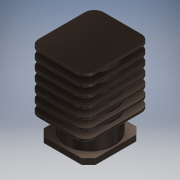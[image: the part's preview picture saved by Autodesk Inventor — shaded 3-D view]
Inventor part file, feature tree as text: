
AUTODESK INVENTOR PART (.ipt)
format: ipt  version: 2019 (Build 230136000, 136)  size: 236,544 bytes
history: native  units: mm
features: extrude x4, sketch x4, pattern_linear x1
ambient origin geometry x8: Origin, YZ Plane, XZ Plane, XY Plane, X Axis, Y Axis, Z Axis, Center Point
bodies: Solid1 (feature_tree)
feature tree (9):
  extrude  "Extrusion1"  Depth=8000.0mm TaperAngle=0.0deg
  extrude  "Extrusion2"  Depth=1000.0mm
  extrude  "Extrusion3"  Depth=8600.0mm TaperAngle=0.0deg
  pattern_linear  "Rectangular Pattern1"  [2 undecoded]
  extrude  "Extrusion4"  [1 undecoded]
  sketch  "Sketch1"  dims[d6=600.0mm d7=0.0mm d9=8000.0mm d10=0.0mm]
  sketch  "Sketch2"  dims[d24=250.0mm d25=0.0mm d26=70.0mm d28=1000.0mm]
  sketch  "Sketch4"  dims[d29=4700.0mm d30=8600.0mm d31=0.0mm]
  sketch  "Sketch5"
note: 3 required parameter values undecoded (feature->parameter linkage not recoverable at this tier; creation-order binding heuristic only, values carry confidence <= 0.55)
